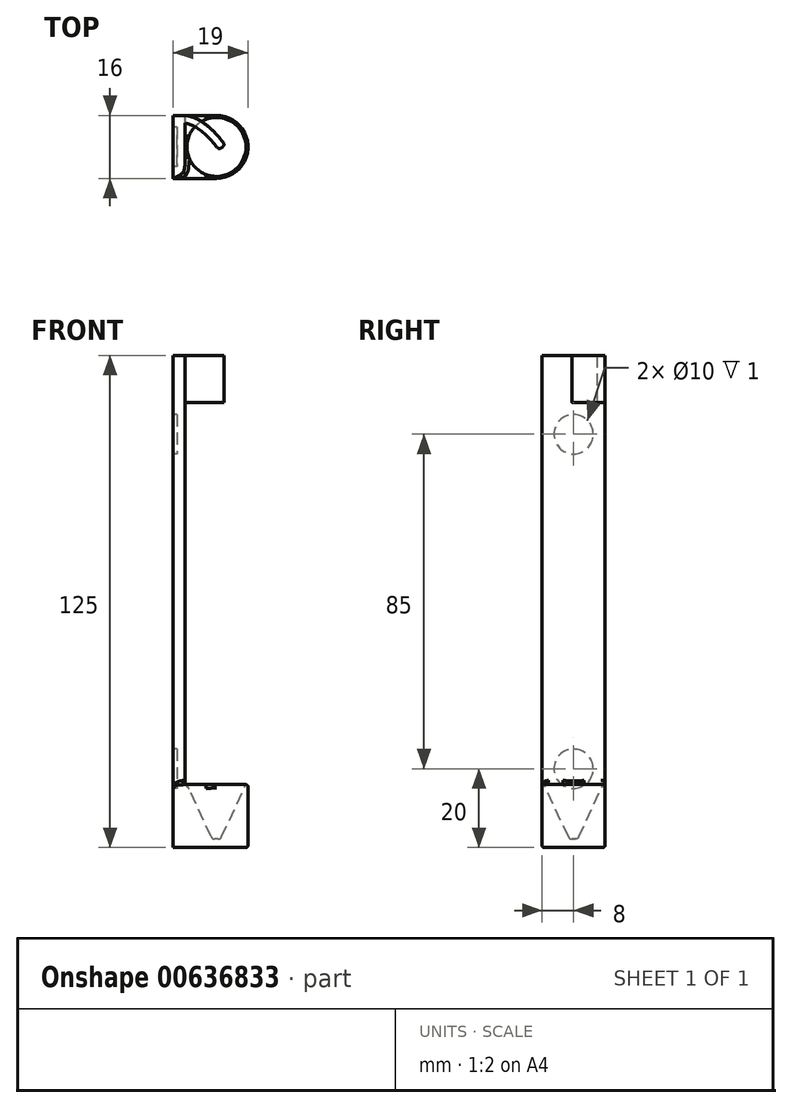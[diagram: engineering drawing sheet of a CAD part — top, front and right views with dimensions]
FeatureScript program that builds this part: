
annotation { "Feature Type Name" : "Feature", "Feature Type Description" : "" }
export const myFeature = defineFeature(function(context is Context, id is Id, definition is map)
    precondition{}
    {
        {
            var Q0;
            Q0=qCreatedBy(makeId("Right.planeOp"),FACE);
            var sketch = newSketch(context, id + "F0", { "sketchPlane" : qUnion([Q0])});
            skLineSegment(sketch, "E0.bottom", {"start": v(0, 0) * mm, "end": v(16, 0) * mm});
            skLineSegment(sketch, "E0.top", {"start": v(0, 125) * mm, "end": v(16, 125) * mm});
            skLineSegment(sketch, "E0.left", {"start": v(0, 0) * mm, "end": v(0, 125) * mm});
            skLineSegment(sketch, "E0.right", {"start": v(16, 0) * mm, "end": v(16, 125) * mm});
            skSolve(sketch);
        }
        {
            var Q0;
            Q0=makeQuery(id+"F0.imprint","IMPRINT",FACE,{"disambiguationData":[TD([[makeQuery(id+"F0.imprint","IMPRINT",EDGE,{"derivedFrom":sQuery(id+"F0.wireOp",EDGE,"E0.bottom")}),1.0]])]});
            extrude(context, id + "F1", {"entities" : qUnion([Q0]), "depth" : 3 * mm, "offsetDistance" : 25 * mm});
        }
        {
            var Q0;
            Q0=makeQuery(id+"F1.opExtrude","CAP_FACE",FACE,{"disambiguationData":[OSD([sQuery(id+"F0.wireOp",EDGE,"E0.bottom"),sQuery(id+"F0.wireOp",EDGE,"E0.top"),sQuery(id+"F0.wireOp",EDGE,"E0.left"),sQuery(id+"F0.wireOp",EDGE,"E0.right")])],"isStart":false});
            var sketch = newSketch(context, id + "F2", { "sketchPlane" : qUnion([Q0])});
            skLineSegment(sketch, "E1.bottom", {"start": v(16, 0) * mm, "end": v(0, 0) * mm});
            skLineSegment(sketch, "E1.top", {"start": v(16, 16) * mm, "end": v(0, 16) * mm});
            skLineSegment(sketch, "E1.left", {"start": v(16, 0) * mm, "end": v(16, 16) * mm});
            skLineSegment(sketch, "E1.right", {"start": v(0, 0) * mm, "end": v(0, 16) * mm});
            skSolve(sketch);
        }
        {
            var Q0;
            Q0=makeQuery(id+"F2.imprint","IMPRINT",FACE,{"disambiguationData":[TD([[makeQuery(id+"F2.imprint","IMPRINT",EDGE,{"derivedFrom":sQuery(id+"F2.wireOp",EDGE,"E1.bottom")}),1.0]])]});
            extrude(context, id + "F3", {"entities" : qUnion([Q0]), "operationType" : NewBodyOperationType.ADD, "depth" : 16 * mm, "offsetDistance" : 25 * mm});
        }
        {
            var Q0;
            Q0=makeQuery(id+"F3.opExtrude","SWEPT_FACE",FACE,{"disambiguationData":[OSD([sQuery(id+"F2.wireOp",EDGE,"E1.top")])]});
            var sketch = newSketch(context, id + "F4", { "sketchPlane" : qUnion([Q0])});
            skLineSegment(sketch, "E2", {"start": v(19, 0) * mm, "end": v(3, 16) * mm, "construction": true});
            skLineSegment(sketch, "E3", {"start": v(3, 0) * mm, "end": v(19, 16) * mm, "construction": true});
            skCircle(sketch, "E4", {"center": v(11, 8) * mm, "radius": 7.5 * mm});
            skSolve(sketch);
        }
        {
            var Q0;
            Q0=makeQuery(id+"F4.imprint","IMPRINT",FACE,{"disambiguationData":[TD([[makeQuery(id+"F4.imprint","IMPRINT",EDGE,{"derivedFrom":sQuery(id+"F4.wireOp",EDGE,"E4")}),1.0]])]});
            extrude(context, id + "F5", {"entities" : qUnion([Q0]), "operationType" : NewBodyOperationType.REMOVE, "oppositeDirection" : true, "depth" : 13.8 * mm, "offsetDistance" : 25 * mm, "hasDraft" : true, "draftAngle" : 25 * degree, "draftPullDirection" : true});
        }
        {
            var Q0;
            Q0=makeQuery(id+"F1.opExtrude","CAP_FACE",FACE,{"disambiguationData":[OSD([sQuery(id+"F0.wireOp",EDGE,"E0.bottom"),sQuery(id+"F0.wireOp",EDGE,"E0.top"),sQuery(id+"F0.wireOp",EDGE,"E0.left"),sQuery(id+"F0.wireOp",EDGE,"E0.right")])],"isStart":false});
            var sketch = newSketch(context, id + "F6", { "sketchPlane" : qUnion([Q0])});
            skLineSegment(sketch, "E5.bottom", {"start": v(16, 125) * mm, "end": v(14, 125) * mm});
            skLineSegment(sketch, "E5.top", {"start": v(16, 113) * mm, "end": v(14, 113) * mm});
            skLineSegment(sketch, "E5.left", {"start": v(16, 125) * mm, "end": v(16, 113) * mm});
            skLineSegment(sketch, "E5.right", {"start": v(14, 125) * mm, "end": v(14, 113) * mm});
            skSolve(sketch);
        }
        {
            var Q0;
            Q0=makeQuery(id+"F1.opExtrude","SWEPT_FACE",FACE,{"disambiguationData":[OSD([sQuery(id+"F0.wireOp",EDGE,"E0.top")])]});
            var sketch = newSketch(context, id + "F7", { "sketchPlane" : qUnion([Q0])});
            skFitSpline(sketch, "E6", {"points": [v(3, 16) * mm, v(13.17, 8.55) * mm], "startDerivative": vector(11.46, -0.72) * mm, "endDerivative": vector(7.56, -10.18) * mm});
            skSolve(sketch);
        }
        {
            var Q0;
            Q0=makeQuery(id+"F6.imprint","IMPRINT",FACE,{"disambiguationData":[TD([[makeQuery(id+"F6.imprint","IMPRINT",EDGE,{"derivedFrom":sQuery(id+"F6.wireOp",EDGE,"E5.bottom")}),-1.0]])]});
            var Q1;
            Q1=sQuery(id+"F7.wireOp",EDGE,"E6");
            sweep(context, id + "F8", {"operationType" : NewBodyOperationType.ADD, "profiles" : qUnion([Q0]), "path" : qUnion([Q1])});
        }
        {
            var Q0;
            Q0=makeQuery(id+"F1.opExtrude","CAP_FACE",FACE,{"disambiguationData":[OSD([sQuery(id+"F0.wireOp",EDGE,"E0.bottom"),sQuery(id+"F0.wireOp",EDGE,"E0.top"),sQuery(id+"F0.wireOp",EDGE,"E0.left"),sQuery(id+"F0.wireOp",EDGE,"E0.right")])],"isStart":true});
            var sketch = newSketch(context, id + "F9", { "sketchPlane" : qUnion([Q0])});
            skLineSegment(sketch, "E7", {"start": v(-8, -3.47) * mm, "end": v(-8, 142.06) * mm, "construction": true});
            skPoint(sketch, "E7.startSnap0", {"position": v(-8, 0) * mm});
            skCircle(sketch, "E8", {"center": v(-8, 20) * mm, "radius": 5 * mm});
            skCircle(sketch, "E9", {"center": v(-8, 105) * mm, "radius": 5 * mm});
            skSolve(sketch);
        }
        {
            var Q0;
            Q0=makeQuery(id+"F9.imprint","IMPRINT",FACE,{"disambiguationData":[TD([[makeQuery(id+"F9.imprint","IMPRINT",EDGE,{"derivedFrom":sQuery(id+"F9.wireOp",EDGE,"E8")}),1.0]])]});
            var Q1;
            Q1=makeQuery(id+"F9.imprint","IMPRINT",FACE,{"disambiguationData":[TD([[makeQuery(id+"F9.imprint","IMPRINT",EDGE,{"derivedFrom":sQuery(id+"F9.wireOp",EDGE,"E9")}),1.0]])]});
            extrude(context, id + "F10", {"entities" : qUnion([Q0, Q1]), "operationType" : NewBodyOperationType.REMOVE, "oppositeDirection" : true, "depth" : 1 * mm, "offsetDistance" : 25 * mm});
        }
        {
            var Q0;
            Q0=makeQuery(id+"F3.opExtrude","CAP_EDGE",EDGE,{"disambiguationData":[OSD([sQuery(id+"F2.wireOp",EDGE,"E1.right")])],"isStart":false});
            var Q1;
            Q1=makeQuery(id+"F3.opExtrude","CAP_EDGE",EDGE,{"disambiguationData":[OSD([sQuery(id+"F2.wireOp",EDGE,"E1.left")])],"isStart":false});
            fillet(context, id + "F11", {"entities" : qUnion([Q0, Q1]), "radius" : 8 * mm, "tangentPropagation" : true, "allowEdgeOverflow" : false});
        }
        {
            var Q0;
            Q0=makeQuery(id+"F3.boolean.opBoolean","MERGE",EDGE,{"derivedFrom":[makeQuery(id+"F1.opExtrude","SWEPT_EDGE",EDGE,{"disambiguationData":[OSD([sQuery(id+"F0.wireOp",EDGE,"E0.bottom"),sQuery(id+"F0.wireOp",EDGE,"E0.left")])]}),makeQuery(id+"F3.opExtrude","SWEPT_EDGE",EDGE,{"disambiguationData":[OSD([sQuery(id+"F2.wireOp",EDGE,"E1.bottom"),sQuery(id+"F2.wireOp",EDGE,"E1.right")])]})]});
            var Q1;
            Q1=makeQuery(id+"F3.opExtrude","SWEPT_EDGE",EDGE,{"disambiguationData":[OSD([sQuery(id+"F0.wireOp",EDGE,"E0.left"),sQuery(id+"F2.wireOp",EDGE,"E1.top"),sQuery(id+"F2.wireOp",EDGE,"E1.right")])]});
            var Q2;
            Q2=makeQuery(id+"F5.boolean.opBoolean","COPY",EDGE,{"derivedFrom":makeQuery(id+"F5.opExtrude","CAP_EDGE",EDGE,{"disambiguationData":[OSD([sQuery(id+"F4.wireOp",EDGE,"E4")])],"isStart":true})});
            var Q3;
            Q3=makeQuery(id+"F5.boolean.opBoolean","COPY",EDGE,{"derivedFrom":makeQuery(id+"F5.opExtrude","CAP_EDGE",EDGE,{"disambiguationData":[OSD([sQuery(id+"F4.wireOp",EDGE,"E4")])],"isStart":false})});
            fillet(context, id + "F12", {"entities" : qUnion([Q0, Q1, Q2, Q3]), "radius" : 1 * mm, "tangentPropagation" : true, "rho" : 0.7, "crossSection" : FilletCrossSection.CONIC, "allowEdgeOverflow" : false});
        }
        {
            var Q0;
            Q0=makeQuery(id+"F1.opExtrude","CAP_EDGE",EDGE,{"disambiguationData":[OSD([sQuery(id+"F0.wireOp",EDGE,"E0.left")])],"isStart":false});
            fillet(context, id + "F13", {"entities" : qUnion([Q0]), "radius" : 5 * mm, "tangentPropagation" : true, "rho" : .7, "crossSection" : FilletCrossSection.CONIC, "allowEdgeOverflow" : false});
        }
        {
            var Q0;
            Q0=makeQuery(id+"F8.opSweep","CAP_EDGE",EDGE,{"disambiguationData":[OSD([sQuery(id+"F6.wireOp",EDGE,"E5.right"),sQuery(id+"F7.wireOp",VERTEX,"E6.end")])],"isStart":false});
            var Q1;
            Q1=makeQuery(id+"F8.opSweep","CAP_EDGE",EDGE,{"disambiguationData":[OSD([sQuery(id+"F6.wireOp",EDGE,"E5.left"),sQuery(id+"F7.wireOp",VERTEX,"E6.end")])],"isStart":false});
            fillet(context, id + "F14", {"entities" : qUnion([Q0, Q1]), "radius" : 0.89 * mm, "tangentPropagation" : true, "rho" : 0.5, "crossSection" : FilletCrossSection.CONIC, "allowEdgeOverflow" : false});
        }
        {
            var Q0;
            Q0=makeQuery(id+"F13.opFillet","BLEND_EDGE",EDGE,{"blendedFrom":[makeQuery(id+"F1.opExtrude","CAP_EDGE",EDGE,{"disambiguationData":[OSD([sQuery(id+"F0.wireOp",EDGE,"E0.left")])],"isStart":false}),makeQuery(id+"F3.opExtrude","SWEPT_FACE",FACE,{"disambiguationData":[OSD([sQuery(id+"F2.wireOp",EDGE,"E1.top")])]})],"blendedInto":[makeQuery(id+"F3.opExtrude","SWEPT_FACE",FACE,{"disambiguationData":[OSD([sQuery(id+"F2.wireOp",EDGE,"E1.top")])]})]});
            var Q1;
            Q1=makeQuery(id+"F3.opExtrude","CAP_EDGE",EDGE,{"disambiguationData":[OSD([sQuery(id+"F2.wireOp",EDGE,"E1.top")])],"isStart":true});
            var Q2;
            {var subQ0=sQuery(id+"F0.wireOp",EDGE,"E0.right");Q2=makeQuery(id+"F12.opFillet","BLEND_EDGE",EDGE,{"blendedFrom":[makeQuery(id+"F3.opExtrude","SWEPT_EDGE",EDGE,{"disambiguationData":[OSD([subQ0,sQuery(id+"F2.wireOp",EDGE,"E1.top"),sQuery(id+"F2.wireOp",EDGE,"E1.left")])]}),makeQuery(id+"F1.opExtrude","CAP_FACE",FACE,{"disambiguationData":[OSD([sQuery(id+"F0.wireOp",EDGE,"E0.bottom"),sQuery(id+"F0.wireOp",EDGE,"E0.top"),sQuery(id+"F0.wireOp",EDGE,"E0.left"),subQ0])],"isStart":false})],"blendedInto":[makeQuery(id+"F1.opExtrude","CAP_FACE",FACE,{"disambiguationData":[OSD([sQuery(id+"F0.wireOp",EDGE,"E0.bottom"),sQuery(id+"F0.wireOp",EDGE,"E0.top"),sQuery(id+"F0.wireOp",EDGE,"E0.left"),subQ0])],"isStart":false})]});}
            var Q3;
            {var subQ0=sQuery(id+"F0.wireOp",EDGE,"E0.left");Q3=makeQuery(id+"F13.opFillet","BLEND_EDGE",EDGE,{"blendedFrom":[makeQuery(id+"F1.opExtrude","CAP_EDGE",EDGE,{"disambiguationData":[OSD([subQ0])],"isStart":false}),makeQuery(id+"F12.opFillet","BLEND_FACE",FACE,{"disambiguationData":[OSD([subQ0,sQuery(id+"F2.wireOp",EDGE,"E1.top"),sQuery(id+"F2.wireOp",EDGE,"E1.right")])]})],"blendedInto":[makeQuery(id+"F12.opFillet","BLEND_FACE",FACE,{"disambiguationData":[OSD([subQ0,sQuery(id+"F2.wireOp",EDGE,"E1.top"),sQuery(id+"F2.wireOp",EDGE,"E1.right")])]})]});}
            fillet(context, id + "F15", {"entities" : qUnion([Q0, Q1, Q2, Q3]), "radius" : 1 * mm, "tangentPropagation" : true, "rho" : 0.7, "crossSection" : FilletCrossSection.CONIC, "allowEdgeOverflow" : false});
        }
    });
